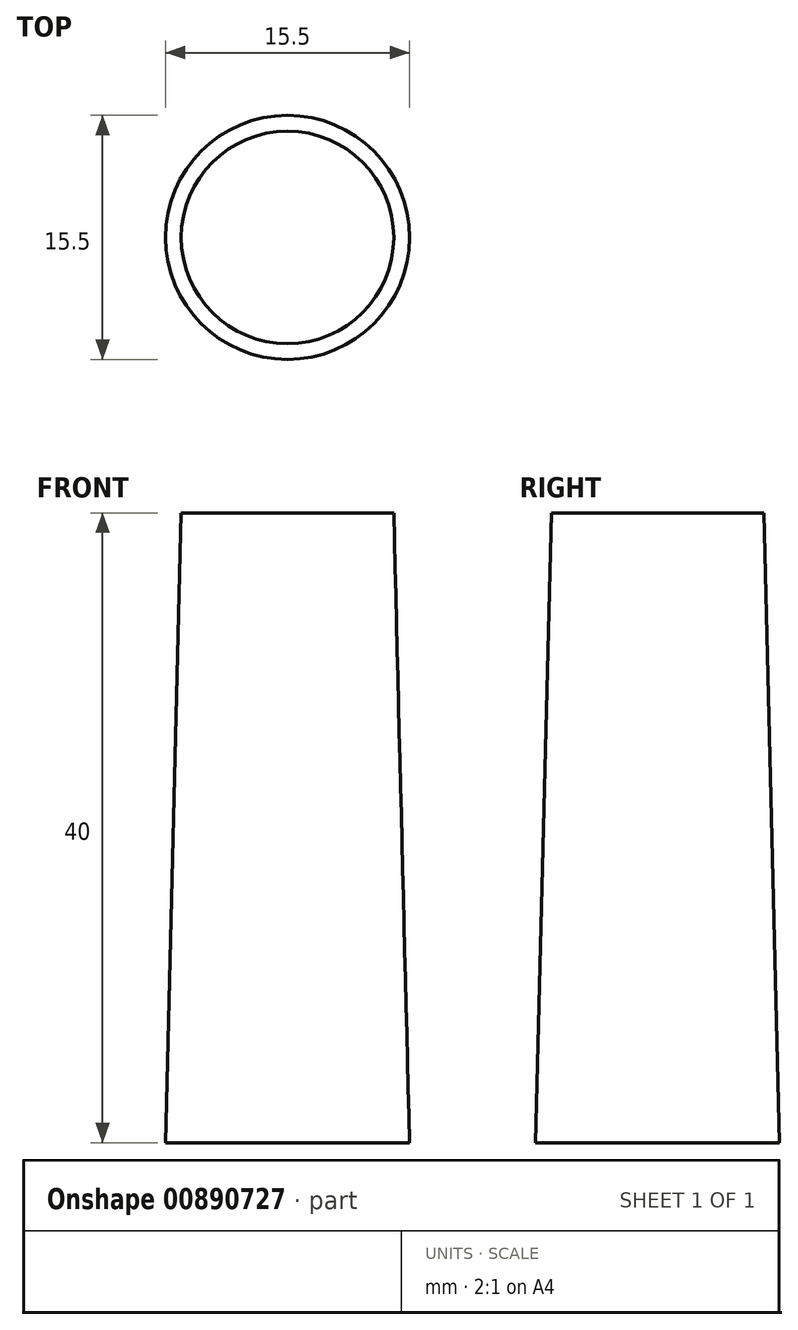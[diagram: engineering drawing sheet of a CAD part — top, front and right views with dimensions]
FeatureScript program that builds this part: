
annotation { "Feature Type Name" : "Feature", "Feature Type Description" : "" }
export const myFeature = defineFeature(function(context is Context, id is Id, definition is map)
    precondition{}
    {
        {
            var Q0;
            Q0=qCreatedBy(makeId("Front.planeOp"),FACE);
            var sketch = newSketch(context, id + "F0", { "sketchPlane" : qUnion([Q0])});
            skLineSegment(sketch, "E0", {"start": v(0, 0) * mm, "end": v(-7.75, 0) * mm});
            skLineSegment(sketch, "E1", {"start": v(-7.75, 0) * mm, "end": v(-6.75, 40) * mm});
            skLineSegment(sketch, "E2", {"start": v(-6.75, 40) * mm, "end": v(0, 40) * mm});
            skLineSegment(sketch, "E3", {"start": v(0, 40) * mm, "end": v(0, 0) * mm});
            skSolve(sketch);
        }
        {
            var Q0;
            Q0=makeQuery(id+"F0.imprint","IMPRINT",FACE,{"disambiguationData":[TD([[makeQuery(id+"F0.imprint","IMPRINT",EDGE,{"derivedFrom":sQuery(id+"F0.wireOp",EDGE,"E0")}),-1.0]])]});
            var Q1;
            Q1=sQuery(id+"F0.wireOp",EDGE,"E3");
            revolve(context, id + "F1", {"surfaceOperationType" : NewSurfaceOperationType.NEW, "entities" : qUnion([Q0]), "axis" : qUnion([Q1]), "revolveType" : RevolveType.FULL});
        }
    });
